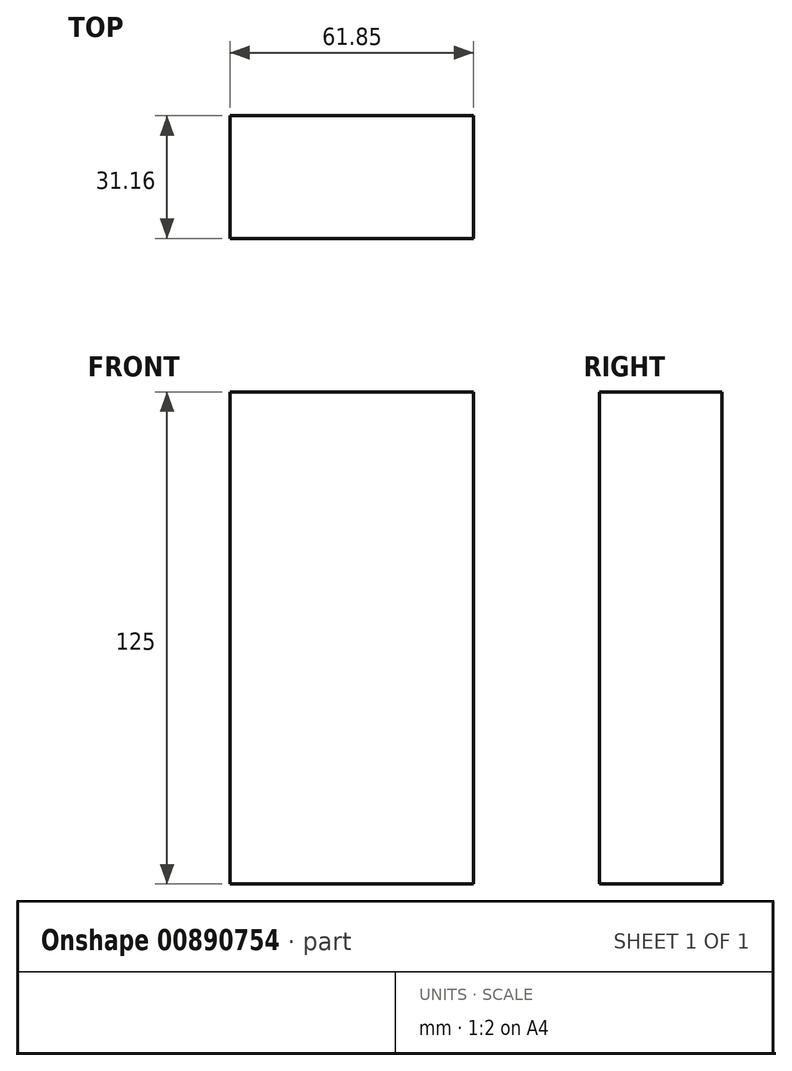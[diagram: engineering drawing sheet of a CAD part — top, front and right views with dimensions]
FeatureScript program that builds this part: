
annotation { "Feature Type Name" : "Feature", "Feature Type Description" : "" }
export const myFeature = defineFeature(function(context is Context, id is Id, definition is map)
    precondition{}
    {
        {
            var Q0;
            Q0=qCreatedBy(makeId("Top.planeOp"),FACE);
            var sketch = newSketch(context, id + "F0", { "sketchPlane" : qUnion([Q0])});
            skLineSegment(sketch, "E0.bottom", {"start": v(0, 0) * mm, "end": v(-61.85, 0) * mm});
            skLineSegment(sketch, "E0.top", {"start": v(0, -31.16) * mm, "end": v(-61.85, -31.16) * mm});
            skLineSegment(sketch, "E0.left", {"start": v(0, 0) * mm, "end": v(0, -31.16) * mm});
            skLineSegment(sketch, "E0.right", {"start": v(-61.85, 0) * mm, "end": v(-61.85, -31.16) * mm});
            skSolve(sketch);
        }
        {
            var Q0;
            Q0=makeQuery(id+"F0.imprint","IMPRINT",FACE,{"disambiguationData":[TD([[makeQuery(id+"F0.imprint","IMPRINT",EDGE,{"derivedFrom":sQuery(id+"F0.wireOp",EDGE,"E0.bottom")}),1.0]])]});
            extrude(context, id + "F1", {"entities" : qUnion([Q0]), "depth" : 25 * mm, "offsetDistance" : 25 * mm});
        }
        {
            var Q0;
            Q0=makeQuery(id+"F0.imprint","IMPRINT",FACE,{"disambiguationData":[TD([[makeQuery(id+"F0.imprint","IMPRINT",EDGE,{"derivedFrom":sQuery(id+"F0.wireOp",EDGE,"E0.bottom")}),1.0]])]});
            extrude(context, id + "F2", {"entities" : qUnion([Q0]), "operationType" : NewBodyOperationType.ADD, "oppositeDirection" : true, "depth" : 100 * mm, "offsetDistance" : 25 * mm});
        }
    });
